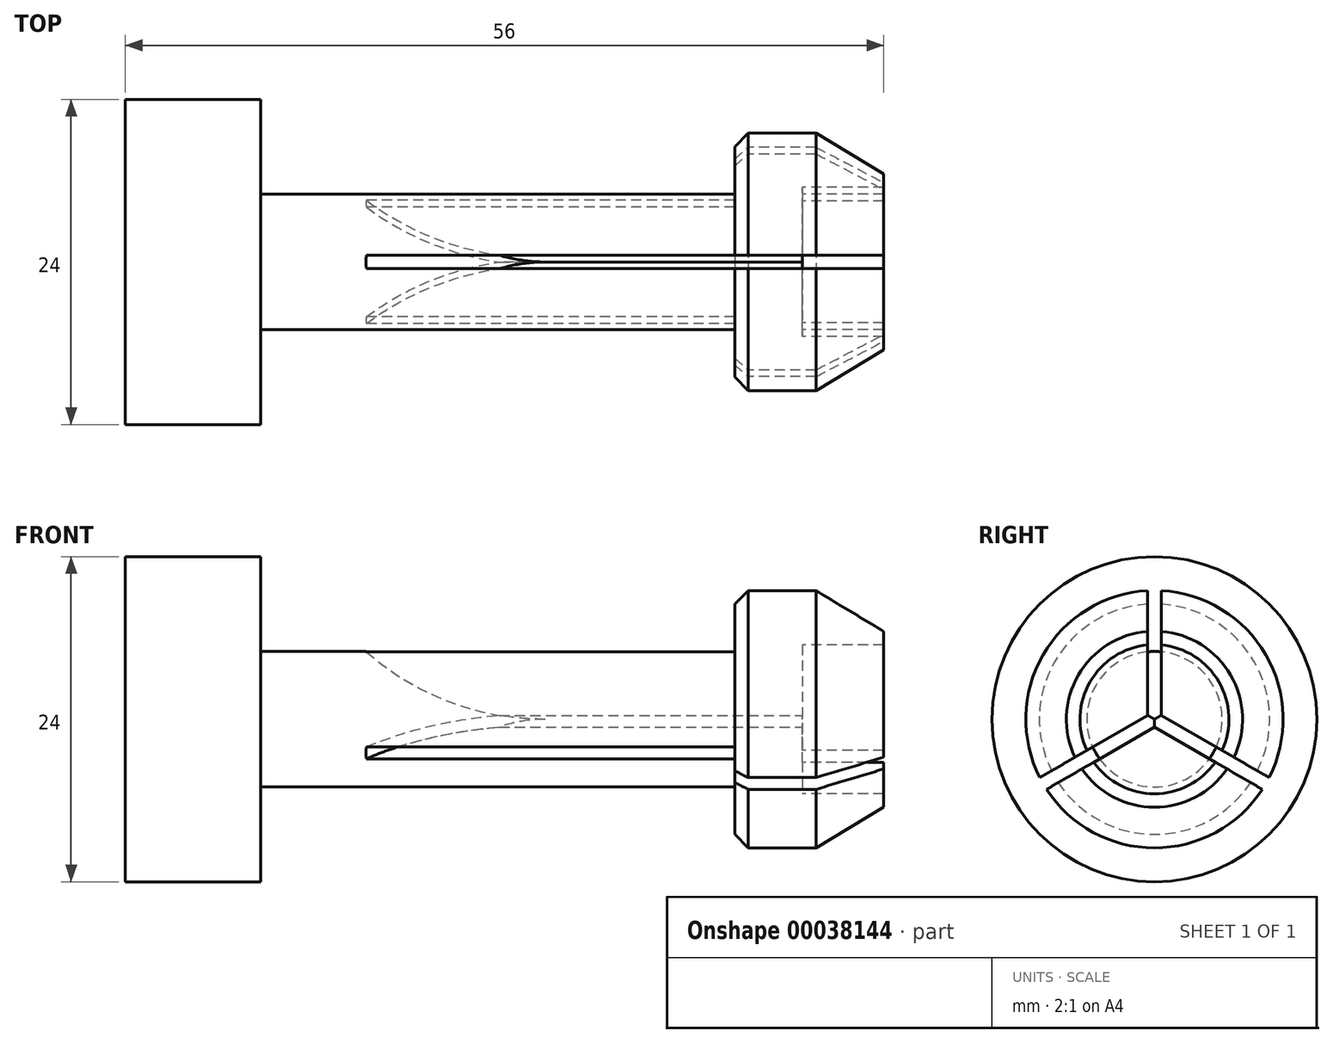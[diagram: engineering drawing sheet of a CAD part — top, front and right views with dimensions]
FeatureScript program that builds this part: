
annotation { "Feature Type Name" : "Feature", "Feature Type Description" : "" }
export const myFeature = defineFeature(function(context is Context, id is Id, definition is map)
    precondition{}
    {
        {
            var Q0;
            Q0=qCreatedBy(makeId("Front.planeOp"),FACE);
            var sketch = newSketch(context, id + "F0", { "sketchPlane" : qUnion([Q0])});
            skLineSegment(sketch, "E0", {"start": v(0, 5) * mm, "end": v(35, 5) * mm});
            skLineSegment(sketch, "E1", {"start": v(35, 5) * mm, "end": v(35, 9.5) * mm});
            skLineSegment(sketch, "E2", {"start": v(35, 9.5) * mm, "end": v(41, 9.5) * mm});
            skLineSegment(sketch, "E3", {"start": v(46, 6.5) * mm, "end": v(46, 5.5) * mm});
            skLineSegment(sketch, "E4", {"start": v(46, 5.5) * mm, "end": v(40, 5.5) * mm});
            skLineSegment(sketch, "E5", {"start": v(40, 5.5) * mm, "end": v(40, 0) * mm});
            skLineSegment(sketch, "E6", {"start": v(40, 0) * mm, "end": v(0, 0) * mm});
            skLineSegment(sketch, "E7", {"start": v(0, 0) * mm, "end": v(46.89, 0) * mm, "construction": true});
            skLineSegment(sketch, "E8", {"start": v(41, 9.5) * mm, "end": v(46, 6.5) * mm});
            skLineSegment(sketch, "E9", {"start": v(0, 5) * mm, "end": v(0, 12) * mm});
            skLineSegment(sketch, "E10", {"start": v(0, 12) * mm, "end": v(-10, 12) * mm});
            skLineSegment(sketch, "E11", {"start": v(-10, 12) * mm, "end": v(-10, 0) * mm});
            skLineSegment(sketch, "E12", {"start": v(-10, 0) * mm, "end": v(0, 0) * mm});
            skSolve(sketch);
        }
        {
            var Q0;
            Q0=makeQuery(id+"F0.imprint","IMPRINT",FACE,{"disambiguationData":[TD([[makeQuery(id+"F0.imprint","IMPRINT",EDGE,{"derivedFrom":sQuery(id+"F0.wireOp",EDGE,"E0")}),-1.0]])]});
            var Q1;
            Q1=sQuery(id+"F0.wireOp",EDGE,"E7");
            revolve(context, id + "F1", {"entities" : qUnion([Q0]), "axis" : qUnion([Q1]), "revolveType" : RevolveType.FULL});
        }
        {
            var Q0;
            Q0=makeQuery(id+"F1.opRevolve","SWEPT_EDGE",EDGE,{"disambiguationData":[OSD([sQuery(id+"F0.wireOp",EDGE,"E1"),sQuery(id+"F0.wireOp",EDGE,"E2")])]});
            chamfer(context, id + "F2", {"entities" : qUnion([Q0]), "width" : 1 * mm, "tangentPropagation" : true});
        }
        {
            var Q0;
            Q0=qCreatedBy(makeId("Front.planeOp"),FACE);
            var sketch = newSketch(context, id + "F3", { "sketchPlane" : qUnion([Q0])});
            skArc(sketch, "E13", {"start": v(21, 40) * mm, "mid": v(1, 20) * mm, "end": v(21, 0) * mm});
            skLineSegment(sketch, "E14", {"start": v(0, 0) * mm, "end": v(124.91, 0) * mm, "construction": true});
            skLineSegment(sketch, "E15", {"start": v(21, 0) * mm, "end": v(55.39, 0) * mm});
            skLineSegment(sketch, "E16", {"start": v(55.39, 0) * mm, "end": v(55.39, 40) * mm});
            skLineSegment(sketch, "E17", {"start": v(55.39, 40) * mm, "end": v(21, 40) * mm});
            skSolve(sketch);
        }
        {
            var Q0;
            Q0=makeQuery(id+"F3.imprint","IMPRINT",FACE,{"disambiguationData":[TD([[makeQuery(id+"F3.imprint","IMPRINT",EDGE,{"derivedFrom":sQuery(id+"F3.wireOp",EDGE,"E13")}),1.0]])]});
            extrude(context, id + "F4", {"entities" : qUnion([Q0]), "endBound" : BoundingType.SYMMETRIC, "depth" : 1 * mm});
        }
        {
            var Q0;
            Q0=makeQuery(id+"F4.opExtrude","SWEPT_BODY",BODY,{"disambiguationData":[OSD([sQuery(id+"F3.wireOp",EDGE,"E13"),sQuery(id+"F3.wireOp",EDGE,"E15"),sQuery(id+"F3.wireOp",EDGE,"E16"),sQuery(id+"F3.wireOp",EDGE,"E17")])]});
            var Q1;
            Q1=sQuery(id+"F3.wireOp",EDGE,"E14");
            circularPattern(context, id + "F5", {"entities" : qUnion([Q0]), "axis" : qUnion([Q1]), "angle" : 360 * degree, "instanceCount" : 3, "equalSpace" : true});
        }
        {
            var Q0;
            Q0=makeQuery(id+"F4.opExtrude","SWEPT_BODY",BODY,{"disambiguationData":[OSD([sQuery(id+"F3.wireOp",EDGE,"E13"),sQuery(id+"F3.wireOp",EDGE,"E15"),sQuery(id+"F3.wireOp",EDGE,"E16"),sQuery(id+"F3.wireOp",EDGE,"E17")])]});
            var Q1;
            Q1=makeQuery(id+"F5.opPattern","COPY",BODY,{"derivedFrom":makeQuery(id+"F4.opExtrude","SWEPT_BODY",BODY,{"disambiguationData":[OSD([sQuery(id+"F3.wireOp",EDGE,"E13"),sQuery(id+"F3.wireOp",EDGE,"E15"),sQuery(id+"F3.wireOp",EDGE,"E16"),sQuery(id+"F3.wireOp",EDGE,"E17")])]}),"instanceName":"1"});
            var Q2;
            Q2=makeQuery(id+"F5.opPattern","COPY",BODY,{"derivedFrom":makeQuery(id+"F4.opExtrude","SWEPT_BODY",BODY,{"disambiguationData":[OSD([sQuery(id+"F3.wireOp",EDGE,"E13"),sQuery(id+"F3.wireOp",EDGE,"E15"),sQuery(id+"F3.wireOp",EDGE,"E16"),sQuery(id+"F3.wireOp",EDGE,"E17")])]}),"instanceName":"2"});
            var Q3;
            Q3=makeQuery(id+"F1.opRevolve","SWEPT_BODY",BODY,{"disambiguationData":[OSD([sQuery(id+"F0.wireOp",EDGE,"f868a5a4-03d5-4aa1-a47b-474d7ef3e890"),sQuery(id+"F0.wireOp",EDGE,"E0"),sQuery(id+"F0.wireOp",EDGE,"E1"),sQuery(id+"F0.wireOp",EDGE,"E2"),sQuery(id+"F0.wireOp",EDGE,"E3"),sQuery(id+"F0.wireOp",EDGE,"E4"),sQuery(id+"F0.wireOp",EDGE,"E5"),sQuery(id+"F0.wireOp",EDGE,"E6"),sQuery(id+"F0.wireOp",EDGE,"E8")])]});
            booleanBodies(context, id + "F6", {"operationType" : BooleanOperationType.SUBTRACTION, "tools" : qUnion([Q0, Q1, Q2]), "targets" : qUnion([Q3])});
        }
    });
